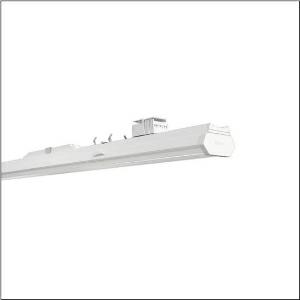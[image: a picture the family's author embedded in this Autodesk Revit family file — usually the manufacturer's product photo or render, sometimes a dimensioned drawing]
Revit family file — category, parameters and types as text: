
# Revit family: licross_r__11_protected_mo_51ts12dn48xf_360d
name_source: partatom
category: Lighting Fixtures
units: mm (PartAtom-declared; Revit-internal decimal feet)

## family parameters
Cut with Voids When Loaded = No
Host = Face
Light Source = No
Part Type = Normal
Room Calculation Point = No
Round Connector Dimension = Use Diameter
Shared = No

## types (1)
- --- (1 x LED, 8470 lm, 56.2 W, 4000K)
    Apparent Load = 56 VA
    CIE Flux Codes = 54 82 95 97 100
    Color Rendering = 80
    Color Temperature = 4000K
    Default Elevation = 1800 mm
    Description = Licross® 11 Protected MOluminaire insert, length: 1.500mm, width: 90mm, height: 101mm, LED rated luminous flux: 8.470lm, light colour: 840, control gear: DALI 2, control gear: ECG DALI, with plug, 5-pole, with phase selection, mains connection: 220..240V, AC, 50/60Hz, halogen-free wiring, primary optical cover: cover, of PMMA, light emission: direct with ceiling illumination distribution, protection rating (complete): IP50, insulation class (complete): insulation class I (protective earthing), certification: CE, ENEC, VDE, protection symbol: D if used in an environment with non-conductive dust loads with corresponding accessories, permissible ambient temperature for indoor applications: -25..+40°C, reducing of maximum allowable ambient temperature of 5°C with ceiling mounting, corresponds to IFS (International Featured Standards) requirements for safety and quality in the food industry, packaging unit: 1 piece
    Height = 92 mm
    Lamp = 1 x LED
    Lamp Light Flux = 8470 lm
    Lamp Power = 56.2 W
    Lamp count = 1
    Length = 1500 mm
    Luminous efficacy = 151 lm/W
    Manufacturer = Siteco
    ModVariant = No
    Model = 51TS12DN48XF
    Mounting Place = Ceiling
    Mounting Type = Pendant
    Number of Poles = 1
    OnlyDefault = Yes
    Power Factor = 1
    Product Name = Licross® 11 Protected MO
    Product group = luminaire insert
    ProductGroupID = 902
    Protection Class = Protection class I
    Protection Degree = IP 50
    RLX_Detail_Level = 1
    RlxData = <blob elided: 23881 chars, md5=705b9ecd>
    Socket = socket
    Standby Power = 0 W
    System Light Flux = 8470 lm
    System Power = 56 W
    Type Comments = factory setting: luminous flux: 100 % | dim-lin: 254 | 370 mA
    Type Image = l_1256145.jpg
    URL = http://relux.com
    VarID = @adj_138145
    Voltage = 0 V
    Weight = 0.00 kg
    Width = 88 mm

## geometry (parser evidence)
native form markers: Blend x4, Sweep x9
no freeform markers — native parametric forms only
